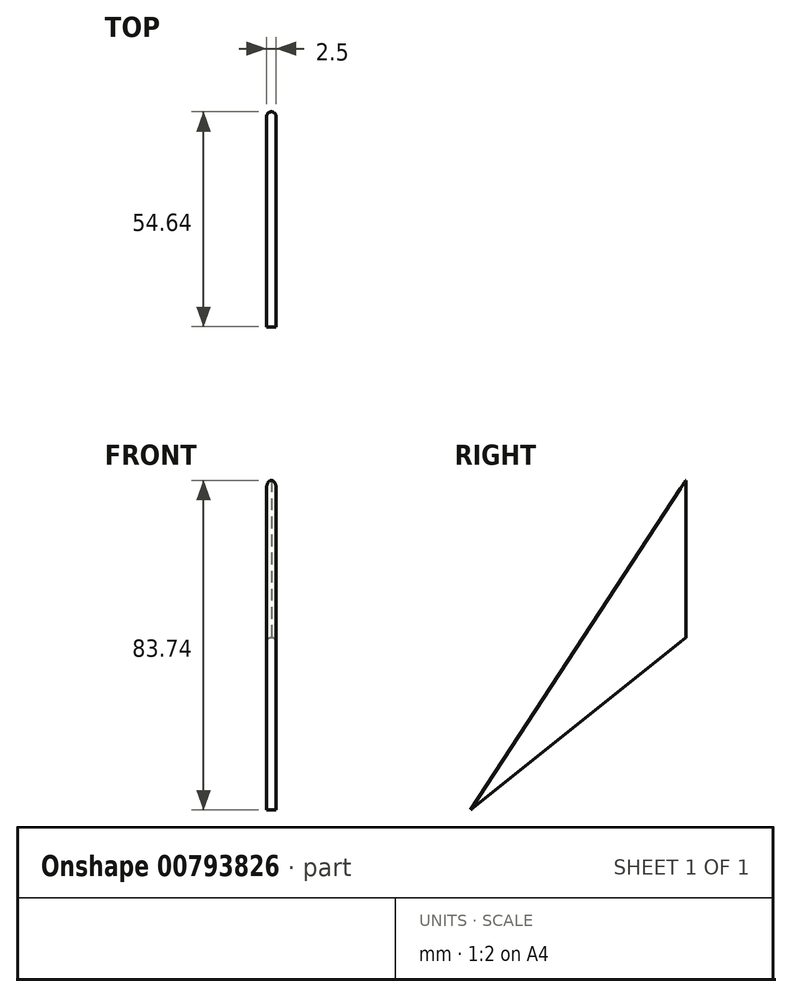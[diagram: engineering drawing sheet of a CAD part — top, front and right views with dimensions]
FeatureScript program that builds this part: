
annotation { "Feature Type Name" : "Feature", "Feature Type Description" : "" }
export const myFeature = defineFeature(function(context is Context, id is Id, definition is map)
    precondition{}
    {
        {
            var Q0;
            Q0=qCreatedBy(makeId("Right.planeOp"),FACE);
            var sketch = newSketch(context, id + "F0", { "sketchPlane" : qUnion([Q0])});
            skLineSegment(sketch, "E0", {"start": v(0, 0) * mm, "end": v(0, 40) * mm});
            skLineSegment(sketch, "E1", {"start": v(0, 40) * mm, "end": v(-54.64, -43.75) * mm});
            skLineSegment(sketch, "E2", {"start": v(-54.64, -43.75) * mm, "end": v(0, 0) * mm});
            skSolve(sketch);
        }
        {
            var Q0;
            Q0 = qSketchRegion(id + "F0", true);
            extrude(context, id + "F1", {"entities" : qUnion([Q0]), "depth" : 2.5 * mm, "offsetDistance" : 25 * mm});
        }
        {
            var Q0;
            Q0=makeQuery(id+"F1.opExtrude","CAP_EDGE",EDGE,{"disambiguationData":[OSD([sQuery(id+"F0.wireOp",EDGE,"E0")])],"isStart":false});
            var Q1;
            Q1=makeQuery(id+"F1.opExtrude","CAP_EDGE",EDGE,{"disambiguationData":[OSD([sQuery(id+"F0.wireOp",EDGE,"E0")])],"isStart":true});
            fillet(context, id + "F2", {"entities" : qUnion([Q0, Q1]), "radius" : 1.35 * mm, "tangentPropagation" : true, "allowEdgeOverflow" : false});
        }
    });
